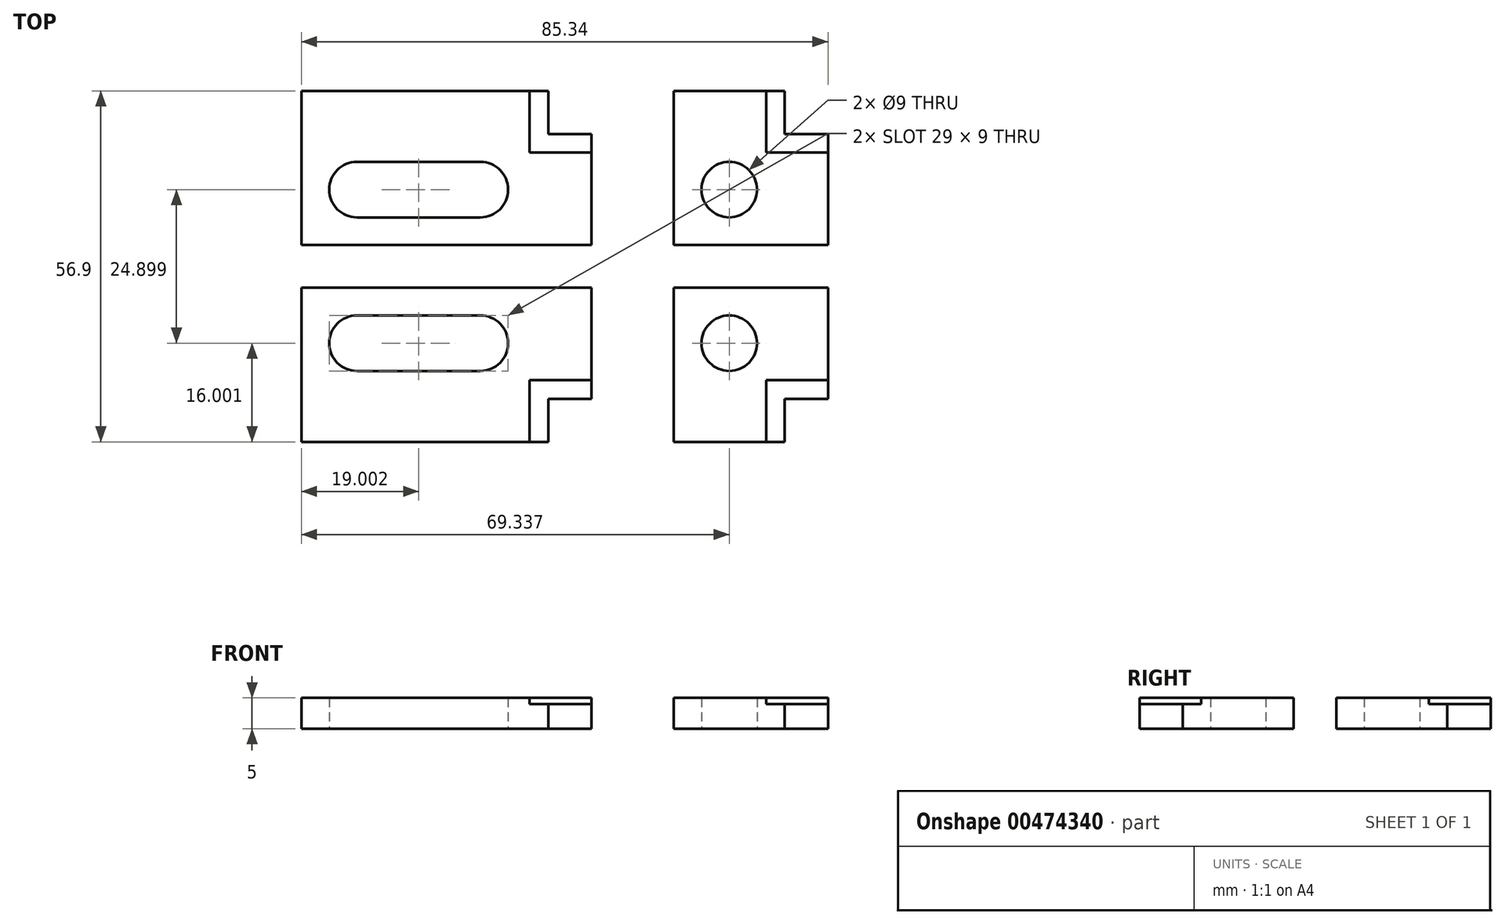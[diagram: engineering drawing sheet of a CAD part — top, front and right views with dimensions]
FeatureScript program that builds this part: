
annotation { "Feature Type Name" : "Feature", "Feature Type Description" : "" }
export const myFeature = defineFeature(function(context is Context, id is Id, definition is map)
    precondition{}
    {
        {
            var Q0;
            Q0=qCreatedBy(makeId("Top.planeOp"),FACE);
            var sketch = newSketch(context, id + "F0", { "sketchPlane" : qUnion([Q0])});
            skLineSegment(sketch, "E0", {"start": v(5.36, 3.45) * mm, "end": v(5.36, 28.45) * mm});
            skLineSegment(sketch, "E1", {"start": v(5.36, 28.45) * mm, "end": v(23.36, 28.45) * mm});
            skLineSegment(sketch, "E2", {"start": v(23.36, 28.45) * mm, "end": v(23.36, 21.45) * mm});
            skLineSegment(sketch, "E3", {"start": v(23.36, 21.45) * mm, "end": v(5.36, 3.45) * mm, "construction": true});
            skLineSegment(sketch, "E4", {"start": v(20.36, 28.45) * mm, "end": v(20.36, 18.45) * mm});
            skCircle(sketch, "E5", {"center": v(14.36, 12.45) * mm, "radius": 4.5 * mm});
            skLineSegment(sketch, "E6.MirrorCS", {"start": v(30.36, 21.45) * mm, "end": v(23.36, 21.45) * mm});
            skLineSegment(sketch, "E7.MirrorCS", {"start": v(30.36, 18.45) * mm, "end": v(20.36, 18.45) * mm});
            skLineSegment(sketch, "E8.MirrorCS", {"start": v(30.36, 3.45) * mm, "end": v(30.36, 21.45) * mm});
            skLineSegment(sketch, "E9.MirrorCS", {"start": v(5.36, 3.45) * mm, "end": v(30.36, 3.45) * mm});
            skLineSegment(sketch, "E10", {"start": v(-7.98, 3.45) * mm, "end": v(-54.98, 3.45) * mm});
            skLineSegment(sketch, "E11", {"start": v(-54.98, 3.45) * mm, "end": v(-54.98, 28.45) * mm});
            skLineSegment(sketch, "E12", {"start": v(-54.98, 28.45) * mm, "end": v(-14.98, 28.45) * mm});
            skLineSegment(sketch, "E13", {"start": v(-14.98, 28.45) * mm, "end": v(-14.98, 21.45) * mm});
            skLineSegment(sketch, "E14", {"start": v(-14.98, 21.45) * mm, "end": v(-7.98, 21.45) * mm});
            skLineSegment(sketch, "E15", {"start": v(-7.98, 21.45) * mm, "end": v(-7.98, 3.45) * mm});
            skLineSegment(sketch, "E16", {"start": v(-17.98, 28.45) * mm, "end": v(-17.98, 18.45) * mm});
            skLineSegment(sketch, "E17", {"start": v(-17.98, 18.45) * mm, "end": v(-7.98, 18.45) * mm});
            skLineSegment(sketch, "E18", {"start": v(-45.98, 16.95) * mm, "end": v(-25.98, 16.95) * mm});
            skLineSegment(sketch, "E19", {"start": v(-25.98, 7.95) * mm, "end": v(-45.98, 7.95) * mm});
            skArc(sketch, "E20", {"start": v(-25.98, 16.95) * mm, "mid": v(-21.48, 12.45) * mm, "end": v(-25.98, 7.95) * mm});
            skArc(sketch, "E21", {"start": v(-45.98, 16.95) * mm, "mid": v(-50.48, 12.45) * mm, "end": v(-45.98, 7.95) * mm});
            skSolve(sketch);
        }
        {
            var Q0;
            {var subQ1=sQuery(id+"F0.wireOp",EDGE,"E10");Q0=makeQuery(id+"F0.imprint","IMPRINT",FACE,{"disambiguationData":[TD([[makeQuery(id+"F0.imprint","IMPRINT",EDGE,{"derivedFrom":subQ1}),-1.0]])]});}
            var Q1;
            {var subQ2=sQuery(id+"F0.wireOp",EDGE,"E0");Q1=makeQuery(id+"F0.imprint","IMPRINT",FACE,{"disambiguationData":[TD([[makeQuery(id+"F0.imprint","IMPRINT",EDGE,{"derivedFrom":subQ2}),-1.0]])]});}
            extrude(context, id + "F1", {"entities" : qUnion([Q0, Q1]), "depth" : 5 * mm});
        }
        {
            var Q0;
            {var subQ3=sQuery(id+"F0.wireOp",EDGE,"E13");Q0=makeQuery(id+"F0.imprint","IMPRINT",FACE,{"disambiguationData":[TD([[makeQuery(id+"F0.imprint","IMPRINT",EDGE,{"derivedFrom":subQ3}),-1.0]])]});}
            var Q1;
            {var subQ2=sQuery(id+"F0.wireOp",EDGE,"E2");Q1=makeQuery(id+"F0.imprint","IMPRINT",FACE,{"disambiguationData":[TD([[makeQuery(id+"F0.imprint","IMPRINT",EDGE,{"derivedFrom":subQ2}),-1.0]])]});}
            extrude(context, id + "F2", {"entities" : qUnion([Q0, Q1]), "operationType" : NewBodyOperationType.ADD, "depth" : 4 * mm});
        }
        {
            var Q0;
            Q0=makeQuery(id+"F1.opExtrude","SWEPT_BODY",BODY,{"disambiguationData":[OSD([sQuery(id+"F0.wireOp",EDGE,"E0"),sQuery(id+"F0.wireOp",EDGE,"E1"),sQuery(id+"F0.wireOp",EDGE,"E4"),sQuery(id+"F0.wireOp",EDGE,"E5"),sQuery(id+"F0.wireOp",EDGE,"E7.MirrorCS"),sQuery(id+"F0.wireOp",EDGE,"E8.MirrorCS"),sQuery(id+"F0.wireOp",EDGE,"E9.MirrorCS")])]});
            var Q1;
            Q1=makeQuery(id+"F1.opExtrude","SWEPT_BODY",BODY,{"disambiguationData":[OSD([sQuery(id+"F0.wireOp",EDGE,"E10"),sQuery(id+"F0.wireOp",EDGE,"E11"),sQuery(id+"F0.wireOp",EDGE,"E12"),sQuery(id+"F0.wireOp",EDGE,"E15"),sQuery(id+"F0.wireOp",EDGE,"E16"),sQuery(id+"F0.wireOp",EDGE,"E17"),sQuery(id+"F0.wireOp",EDGE,"E18"),sQuery(id+"F0.wireOp",EDGE,"E19"),sQuery(id+"F0.wireOp",EDGE,"E20"),sQuery(id+"F0.wireOp",EDGE,"E21")])]});
            var Q2;
            Q2=qCreatedBy(makeId("Front.planeOp"),FACE);
            mirror(context, id + "F3", {"entities" : qUnion([Q0, Q1]), "mirrorPlane" : qUnion([Q2])});
        }
    });
